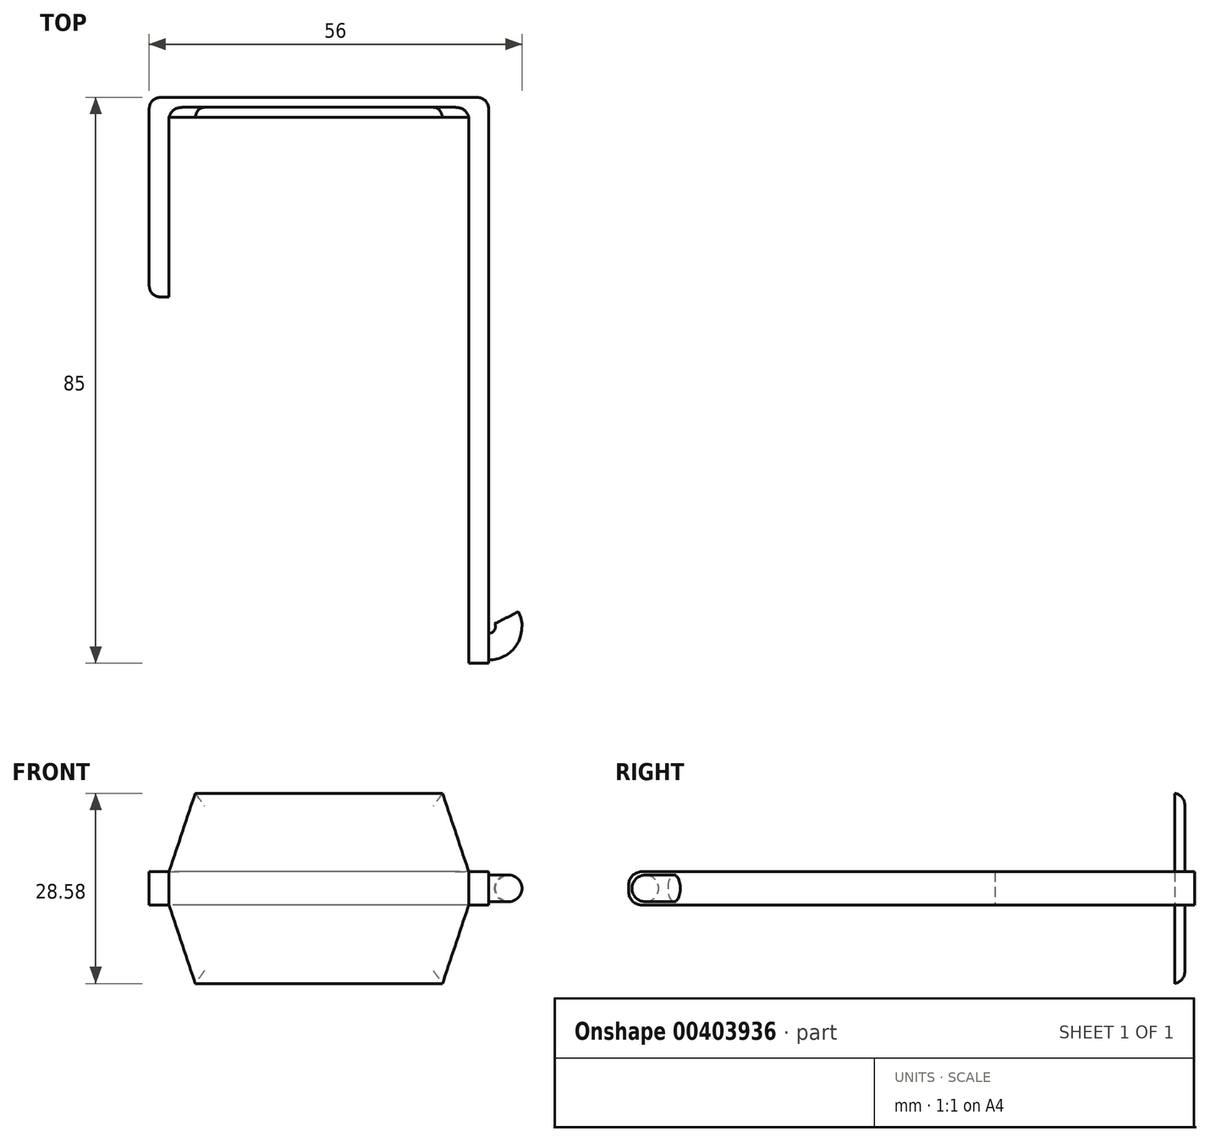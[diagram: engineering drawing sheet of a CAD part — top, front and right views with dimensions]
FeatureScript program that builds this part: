
annotation { "Feature Type Name" : "Feature", "Feature Type Description" : "" }
export const myFeature = defineFeature(function(context is Context, id is Id, definition is map)
    precondition{}
    {
        {
            var Q0;
            Q0=qCreatedBy(makeId("Top.planeOp"),FACE);
            var sketch = newSketch(context, id + "F0", { "sketchPlane" : qUnion([Q0])});
            skLineSegment(sketch, "E0.bottom", {"start": v(1.5, 42.5) * mm, "end": v(-1.5, 42.5) * mm});
            skLineSegment(sketch, "E0.top", {"start": v(1.5, -42.5) * mm, "end": v(-1.5, -42.5) * mm});
            skLineSegment(sketch, "E0.left", {"start": v(1.5, 42.5) * mm, "end": v(1.5, -42.5) * mm});
            skLineSegment(sketch, "E0.right", {"start": v(-1.5, 42.5) * mm, "end": v(-1.5, -42.5) * mm});
            skPoint(sketch, "E0.middle", {"position": v(0, 0) * mm});
            skLineSegment(sketch, "E1.bottom", {"start": v(-1.5, 42.5) * mm, "end": v(-49.5, 42.5) * mm});
            skLineSegment(sketch, "E1.top", {"start": v(-1.5, 39.5) * mm, "end": v(-49.5, 39.5) * mm});
            skLineSegment(sketch, "E1.left", {"start": v(-1.5, 42.5) * mm, "end": v(-1.5, 39.5) * mm});
            skLineSegment(sketch, "E1.right", {"start": v(-49.5, 42.5) * mm, "end": v(-49.5, 39.5) * mm});
            skLineSegment(sketch, "E2.bottom", {"start": v(-49.5, 39.5) * mm, "end": v(-46.5, 39.5) * mm});
            skLineSegment(sketch, "E2.top", {"start": v(-49.5, 12.5) * mm, "end": v(-46.5, 12.5) * mm});
            skLineSegment(sketch, "E2.left", {"start": v(-49.5, 39.5) * mm, "end": v(-49.5, 12.5) * mm});
            skLineSegment(sketch, "E2.right", {"start": v(-46.5, 39.5) * mm, "end": v(-46.5, 12.5) * mm});
            skSolve(sketch);
        }
        {
            var Q0;
            Q0 = qSketchRegion(id + "F0", true);
            extrude(context, id + "F1", {"entities" : qUnion([Q0]), "depth" : 5 * mm});
        }
        {
            var Q0;
            Q0=makeQuery(id+"F1.opExtrude","SWEPT_FACE",FACE,{"disambiguationData":[OSD([sQuery(id+"F0.wireOp",EDGE,"E1.top")])]});
            var sketch = newSketch(context, id + "F2", { "sketchPlane" : qUnion([Q0])});
            skLineSegment(sketch, "E3", {"start": v(-46.5, 2.5) * mm, "end": v(-1.5, 2.5) * mm});
            skLineSegment(sketch, "E4", {"start": v(-1.5, 2.5) * mm, "end": v(-46.5, 2.5) * mm, "construction": true});
            skLineSegment(sketch, "E5", {"start": v(-46.5, 0) * mm, "end": v(-42.56, -11.8) * mm});
            skLineSegment(sketch, "E6", {"start": v(-42.56, -11.8) * mm, "end": v(-24, -11.8) * mm});
            skPoint(sketch, "E6.endSnap0", {"position": v(-24, 0) * mm});
            skLineSegment(sketch, "E7", {"start": v(-24, 2.5) * mm, "end": v(-24, -16.84) * mm, "construction": true});
            skLineSegment(sketch, "E8.MirrorCS", {"start": v(-14, 2.5) * mm, "end": v(-14, -16.84) * mm, "construction": true});
            skLineSegment(sketch, "E9.MirrorCS", {"start": v(-5.44, -11.8) * mm, "end": v(-24, -11.8) * mm});
            skLineSegment(sketch, "E10.MirrorCS", {"start": v(-1.5, 0) * mm, "end": v(-5.44, -11.8) * mm});
            skLineSegment(sketch, "E11.MirrorCS", {"start": v(-46.5, 2.5) * mm, "end": v(-1.5, 2.5) * mm, "construction": true});
            skLineSegment(sketch, "E12.MirrorCS", {"start": v(-46.5, 5) * mm, "end": v(-42.56, 16.8) * mm});
            skLineSegment(sketch, "E13.MirrorCS", {"start": v(-42.56, 16.8) * mm, "end": v(-24, 16.8) * mm});
            skLineSegment(sketch, "E14.MirrorCS", {"start": v(-5.44, 16.8) * mm, "end": v(-24, 16.8) * mm});
            skLineSegment(sketch, "E15.MirrorCS", {"start": v(-1.5, 5) * mm, "end": v(-5.44, 16.8) * mm});
            skSolve(sketch);
        }
        {
            var Q0;
            Q0=makeQuery(id+"F2.imprint","IMPRINT",FACE,{"disambiguationData":[TD([[makeQuery(id+"F2.imprint","IMPRINT",EDGE,{"derivedFrom":sQuery(id+"F2.wireOp",EDGE,"E12.MirrorCS")}),-1.0]])]});
            var Q1;
            Q1=makeQuery(id+"F2.imprint","IMPRINT",FACE,{"disambiguationData":[TD([[makeQuery(id+"F2.imprint","IMPRINT",EDGE,{"derivedFrom":sQuery(id+"F2.wireOp",EDGE,"E5")}),1.0]])]});
            extrude(context, id + "F3", {"entities" : qUnion([Q0, Q1]), "operationType" : NewBodyOperationType.ADD, "oppositeDirection" : true, "depth" : 1.5 * mm});
        }
        {
            var Q0;
            Q0=makeQuery(id+"F1.opExtrude","SWEPT_FACE",FACE,{"disambiguationData":[OSD([sQuery(id+"F0.wireOp",EDGE,"E0.left")])]});
            var sketch = newSketch(context, id + "F4", { "sketchPlane" : qUnion([Q0])});
            skCircle(sketch, "E16", {"center": v(-40, 2.5) * mm, "radius": 2 * mm});
            skPoint(sketch, "E17.startSnap0", {"position": v(-42.5, 2.5) * mm});
            skLineSegment(sketch, "E18", {"start": v(-30.87, 2.5) * mm, "end": v(-42.5, 2.5) * mm, "construction": true});
            skLineSegment(sketch, "E19", {"start": v(-37, 7.8) * mm, "end": v(-37, -3.05) * mm, "construction": true});
            skSolve(sketch);
        }
        {
            var Q0;
            Q0=makeQuery(id+"F4.imprint","IMPRINT",FACE,{"disambiguationData":[TD([[makeQuery(id+"F4.imprint","IMPRINT",EDGE,{"derivedFrom":sQuery(id+"F4.wireOp",EDGE,"E16")}),1.0]])]});
            var Q1;
            Q1 = qSketchRegion(id + "F4", true);
            var Q2;
            Q2=sQuery(id+"F4.wireOp",EDGE,"E19");
            revolve(context, id + "F5", {"operationType" : NewBodyOperationType.ADD, "entities" : qUnion([Q0, Q1]), "axis" : qUnion([Q2]), "revolveType" : RevolveType.ONE_DIRECTION, "oppositeDirection" : true, "angle" : 116.87 * degree});
        }
        {
            var Q0;
            Q0=makeQuery(id+"F1.opExtrude","CAP_EDGE",EDGE,{"disambiguationData":[OSD([sQuery(id+"F0.wireOp",EDGE,"E0.top")])],"isStart":true});
            var Q1;
            Q1=makeQuery(id+"F1.opExtrude","CAP_EDGE",EDGE,{"disambiguationData":[OSD([sQuery(id+"F0.wireOp",EDGE,"E0.top")])],"isStart":false});
            fillet(context, id + "F6", {"entities" : qUnion([Q0, Q1]), "radius" : 2 * mm, "tangentPropagation" : true, "allowEdgeOverflow" : false});
        }
        {
            var Q0;
            Q0=makeQuery(id+"F1.opExtrude","SWEPT_EDGE",EDGE,{"disambiguationData":[OSD([sQuery(id+"F0.wireOp",EDGE,"E0.bottom"),sQuery(id+"F0.wireOp",EDGE,"E0.left")])]});
            var Q1;
            Q1=makeQuery(id+"F1.opExtrude","SWEPT_EDGE",EDGE,{"disambiguationData":[OSD([sQuery(id+"F0.wireOp",EDGE,"E1.bottom"),sQuery(id+"F0.wireOp",EDGE,"E1.right")])]});
            var Q2;
            Q2=makeQuery(id+"F1.opExtrude","SWEPT_EDGE",EDGE,{"disambiguationData":[OSD([sQuery(id+"F0.wireOp",EDGE,"E2.top"),sQuery(id+"F0.wireOp",EDGE,"E2.left")])]});
            var Q3;
            Q3=makeQuery(id+"F3.opExtrude","CAP_EDGE",EDGE,{"disambiguationData":[OSD([sQuery(id+"F2.wireOp",EDGE,"E12.MirrorCS")])],"isStart":false});
            var Q4;
            Q4=makeQuery(id+"F3.opExtrude","CAP_EDGE",EDGE,{"disambiguationData":[OSD([sQuery(id+"F2.wireOp",EDGE,"E13.MirrorCS"),sQuery(id+"F2.wireOp",EDGE,"E14.MirrorCS")])],"isStart":false});
            var Q5;
            Q5=makeQuery(id+"F3.opExtrude","CAP_EDGE",EDGE,{"disambiguationData":[OSD([sQuery(id+"F2.wireOp",EDGE,"E15.MirrorCS")])],"isStart":false});
            var Q6;
            Q6=makeQuery(id+"F3.opExtrude","CAP_EDGE",EDGE,{"disambiguationData":[OSD([sQuery(id+"F2.wireOp",EDGE,"E5")])],"isStart":false});
            var Q7;
            Q7=makeQuery(id+"F3.opExtrude","CAP_EDGE",EDGE,{"disambiguationData":[OSD([sQuery(id+"F2.wireOp",EDGE,"E6"),sQuery(id+"F2.wireOp",EDGE,"E9.MirrorCS")])],"isStart":false});
            var Q8;
            Q8=makeQuery(id+"F3.opExtrude","CAP_EDGE",EDGE,{"disambiguationData":[OSD([sQuery(id+"F2.wireOp",EDGE,"E10.MirrorCS")])],"isStart":false});
            fillet(context, id + "F7", {"entities" : qUnion([Q0, Q1, Q2, Q3, Q4, Q5, Q6, Q7, Q8]), "radius" : 2 * mm, "tangentPropagation" : true, "rho" : 0.5, "crossSection" : FilletCrossSection.CONIC, "allowEdgeOverflow" : false});
        }
    });
